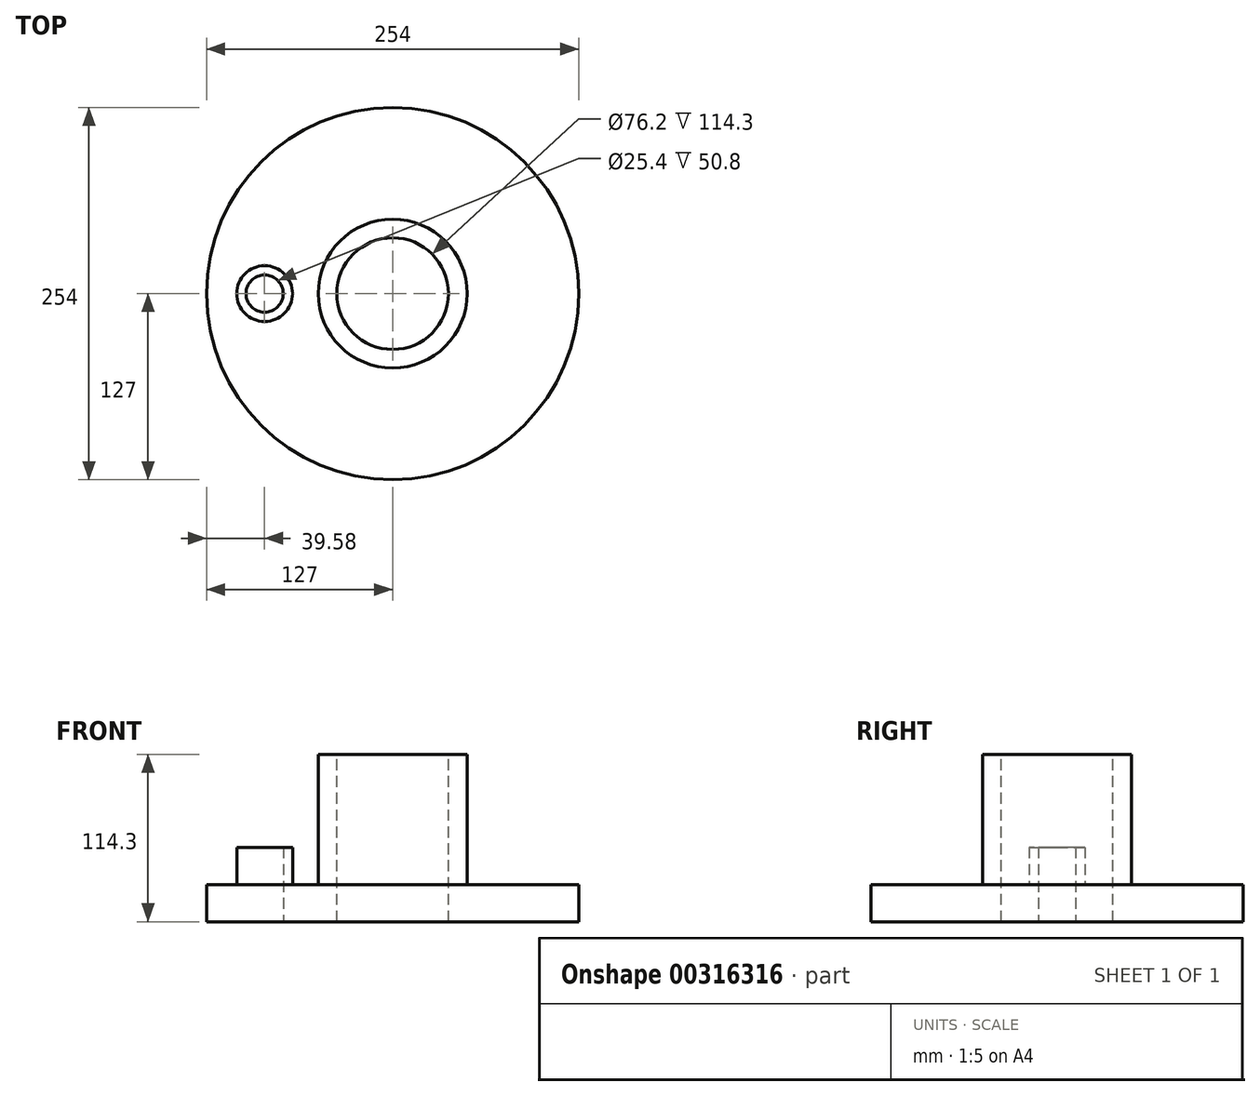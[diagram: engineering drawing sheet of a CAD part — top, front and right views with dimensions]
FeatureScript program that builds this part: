
annotation { "Feature Type Name" : "Feature", "Feature Type Description" : "" }
export const myFeature = defineFeature(function(context is Context, id is Id, definition is map)
    precondition{}
    {
        {
            var Q0;
            Q0=qCreatedBy(makeId("Top.planeOp"),FACE);
            var sketch = newSketch(context, id + "F0", { "sketchPlane" : qUnion([Q0])});
            skCircle(sketch, "E0", {"center": v(0, 0) * mm, "radius": 127 * mm});
            skSolve(sketch);
        }
        {
            var Q0;
            Q0 = qSketchRegion(id + "F0", true);
            extrude(context, id + "F1", {"entities" : qUnion([Q0]), "depth" : 25.4 * mm});
        }
        {
            var Q0;
            Q0=qCreatedBy(makeId("Top.planeOp"),FACE);
            var sketch = newSketch(context, id + "F2", { "sketchPlane" : qUnion([Q0])});
            skCircle(sketch, "E1", {"center": v(0, 0) * mm, "radius": 6.35 * mm});
            skCircle(sketch, "E2", {"center": v(0, 0) * mm, "radius": 50.8 * mm});
            skSolve(sketch);
        }
        {
            var Q0;
            Q0 = qSketchRegion(id + "F2", true);
            extrude(context, id + "F3", {"entities" : qUnion([Q0]), "operationType" : NewBodyOperationType.ADD, "depth" : 114.3 * mm});
        }
        {
            var Q0;
            Q0=makeQuery(id+"F3.opExtrude","CAP_FACE",FACE,{"disambiguationData":[OSD([sQuery(id+"F2.wireOp",EDGE,"E1"),sQuery(id+"F2.wireOp",EDGE,"E2")])],"isStart":false});
            var sketch = newSketch(context, id + "F4", { "sketchPlane" : qUnion([Q0])});
            skCircle(sketch, "E3", {"center": v(0, 0) * mm, "radius": 38.1 * mm});
            skSolve(sketch);
        }
        {
            var Q0;
            Q0 = qSketchRegion(id + "F4", true);
            extrude(context, id + "F5", {"entities" : qUnion([Q0]), "operationType" : NewBodyOperationType.REMOVE, "endBound" : BoundingType.THROUGH_ALL, "oppositeDirection" : true, "depth" : 25.4 * mm});
        }
        {
            var Q0;
            {var subQ0=sQuery(id+"F0.wireOp",EDGE,"E0");Q0=makeQuery(id+"F3.boolean.opBoolean","SPLIT",FACE,{"disambiguationData":[TD([makeQuery(id+"F1.opExtrude","SWEPT_FACE",FACE,{"disambiguationData":[OSD([subQ0])]})])],"derivedFrom":makeQuery(id+"F1.opExtrude","CAP_FACE",FACE,{"disambiguationData":[OSD([subQ0])],"isStart":false})});}
            var sketch = newSketch(context, id + "F6", { "sketchPlane" : qUnion([Q0])});
            skCircle(sketch, "E4", {"center": v(-87.42, 0) * mm, "radius": 19.05 * mm});
            skCircle(sketch, "E5", {"center": v(-87.42, 0) * mm, "radius": 12.7 * mm});
            skSolve(sketch);
        }
        {
            var Q0;
            Q0 = qSketchRegion(id + "F6", true);
            extrude(context, id + "F7", {"entities" : qUnion([Q0]), "operationType" : NewBodyOperationType.ADD, "depth" : 25.4 * mm});
        }
        {
            var Q0;
            {var subQ0=sQuery(id+"F0.wireOp",EDGE,"E0");Q0=makeQuery(id+"F7.boolean.opBoolean","SPLIT",FACE,{"disambiguationData":[TD([makeQuery(id+"F7.opExtrude","SWEPT_FACE",FACE,{"disambiguationData":[OSD([sQuery(id+"F6.wireOp",EDGE,"E5")])]})])],"derivedFrom":makeQuery(id+"F3.boolean.opBoolean","SPLIT",FACE,{"disambiguationData":[TD([makeQuery(id+"F1.opExtrude","SWEPT_FACE",FACE,{"disambiguationData":[OSD([subQ0])]})])],"derivedFrom":makeQuery(id+"F1.opExtrude","CAP_FACE",FACE,{"disambiguationData":[OSD([subQ0])],"isStart":false})})});}
            extrude(context, id + "F8", {"entities" : qUnion([Q0]), "operationType" : NewBodyOperationType.REMOVE, "endBound" : BoundingType.THROUGH_ALL, "oppositeDirection" : true, "depth" : 25.4 * mm});
        }
    });
